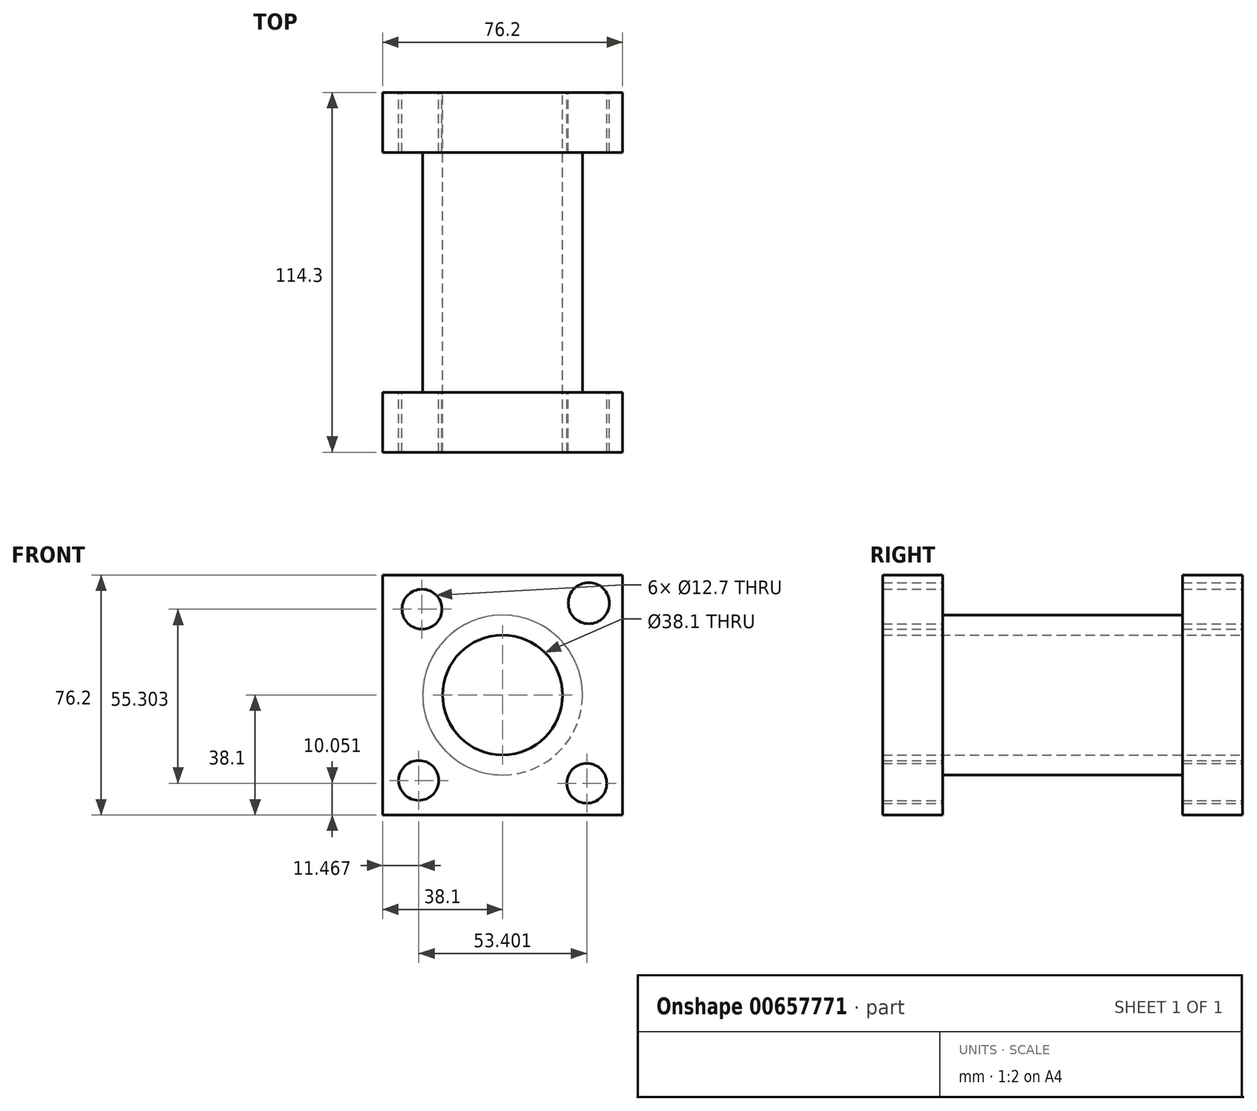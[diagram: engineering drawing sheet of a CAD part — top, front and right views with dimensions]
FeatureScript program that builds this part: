
annotation { "Feature Type Name" : "Feature", "Feature Type Description" : "" }
export const myFeature = defineFeature(function(context is Context, id is Id, definition is map)
    precondition{}
    {
        {
            var Q0;
            Q0=qCreatedBy(makeId("Front.planeOp"),FACE);
            var sketch = newSketch(context, id + "F0", { "sketchPlane" : qUnion([Q0])});
            skLineSegment(sketch, "E0.bottom", {"start": v(38.1, 38.1) * mm, "end": v(-38.1, 38.1) * mm});
            skLineSegment(sketch, "E0.top", {"start": v(38.1, -38.1) * mm, "end": v(-38.1, -38.1) * mm});
            skLineSegment(sketch, "E0.left", {"start": v(38.1, 38.1) * mm, "end": v(38.1, -38.1) * mm});
            skLineSegment(sketch, "E0.right", {"start": v(-38.1, 38.1) * mm, "end": v(-38.1, -38.1) * mm});
            skPoint(sketch, "E0.middle", {"position": v(0, 0) * mm});
            skSolve(sketch);
        }
        {
            var Q0;
            Q0 = qSketchRegion(id + "F0", true);
            extrude(context, id + "F1", {"entities" : qUnion([Q0]), "depth" : 19.05 * mm, "offsetDistance" : 25.4 * mm});
        }
        {
            var Q0;
            Q0=makeQuery(id+"F1.opExtrude","CAP_FACE",FACE,{"disambiguationData":[OSD([sQuery(id+"F0.wireOp",EDGE,"E0.bottom"),sQuery(id+"F0.wireOp",EDGE,"E0.top"),sQuery(id+"F0.wireOp",EDGE,"E0.left"),sQuery(id+"F0.wireOp",EDGE,"E0.right")])],"isStart":false});
            var sketch = newSketch(context, id + "F2", { "sketchPlane" : qUnion([Q0])});
            skCircle(sketch, "E1", {"center": v(0, 0) * mm, "radius": 19.05 * mm});
            skSolve(sketch);
        }
        {
            var Q0;
            Q0=makeQuery(id+"F2.imprint","IMPRINT",FACE,{"disambiguationData":[TD([[makeQuery(id+"F2.imprint","IMPRINT",EDGE,{"derivedFrom":sQuery(id+"F2.wireOp",EDGE,"E1")}),1.0]])]});
            extrude(context, id + "F3", {"entities" : qUnion([Q0]), "operationType" : NewBodyOperationType.ADD, "depth" : 25.4 * mm, "offsetDistance" : 25.4 * mm});
        }
        {
            var Q0;
            Q0=makeQuery(id+"F3.opExtrude","CAP_FACE",FACE,{"disambiguationData":[OSD([sQuery(id+"F2.wireOp",EDGE,"E1")])],"isStart":false});
            var sketch = newSketch(context, id + "F4", { "sketchPlane" : qUnion([Q0])});
            skSolve(sketch);
        }
        {
            var Q0;
            Q0 = qSketchRegion(id + "F4", true);
            var Q1;
            Q1=makeQuery(id+"F4.imprint","IMPRINT",FACE,{"disambiguationData":[TD([[makeQuery(id+"F4.imprint","IMPRINT",EDGE,{"derivedFrom":makeQuery(id+"F3.opExtrude","CAP_EDGE",EDGE,{"disambiguationData":[OSD([sQuery(id+"F2.wireOp",EDGE,"E1")])],"isStart":false})}),1.0]])]});
            extrude(context, id + "F5", {"entities" : qUnion([Q0, Q1]), "operationType" : NewBodyOperationType.ADD, "depth" : 50.8 * mm, "offsetDistance" : 25.4 * mm});
        }
        {
            var Q0;
            Q0=makeQuery(id+"F5.opExtrude","CAP_FACE",FACE,{"disambiguationData":[OSD([sQuery(id+"F2.wireOp",EDGE,"E1")])],"isStart":false});
            var sketch = newSketch(context, id + "F6", { "sketchPlane" : qUnion([Q0])});
            skLineSegment(sketch, "E2.bottom", {"start": v(-38.1, -38.1) * mm, "end": v(38.1, -38.1) * mm});
            skLineSegment(sketch, "E2.top", {"start": v(-38.1, 38.1) * mm, "end": v(38.1, 38.1) * mm});
            skLineSegment(sketch, "E2.left", {"start": v(-38.1, -38.1) * mm, "end": v(-38.1, 38.1) * mm});
            skLineSegment(sketch, "E2.right", {"start": v(38.1, -38.1) * mm, "end": v(38.1, 38.1) * mm});
            skPoint(sketch, "E2.middle", {"position": v(0, 0) * mm});
            skSolve(sketch);
        }
        {
            var Q0;
            Q0 = qSketchRegion(id + "F6", true);
            extrude(context, id + "F7", {"entities" : qUnion([Q0]), "operationType" : NewBodyOperationType.ADD, "depth" : 19.05 * mm, "offsetDistance" : 25.4 * mm});
        }
        {
            var Q0;
            Q0=makeQuery(id+"F7.opExtrude","CAP_FACE",FACE,{"disambiguationData":[OSD([sQuery(id+"F6.wireOp",EDGE,"E2.bottom"),sQuery(id+"F6.wireOp",EDGE,"E2.top"),sQuery(id+"F6.wireOp",EDGE,"E2.left"),sQuery(id+"F6.wireOp",EDGE,"E2.right")])],"isStart":true});
            var sketch = newSketch(context, id + "F8", { "sketchPlane" : qUnion([Q0])});
            skCircle(sketch, "E3", {"center": v(0, 0) * mm, "radius": 25.4 * mm});
            skSolve(sketch);
        }
        {
            var Q0;
            Q0 = qSketchRegion(id + "F8", true);
            extrude(context, id + "F9", {"entities" : qUnion([Q0]), "operationType" : NewBodyOperationType.ADD, "depth" : 76.2 * mm, "offsetDistance" : 25.4 * mm});
        }
        {
            var Q0;
            Q0=makeQuery(id+"F1.opExtrude","CAP_FACE",FACE,{"disambiguationData":[OSD([sQuery(id+"F0.wireOp",EDGE,"E0.bottom"),sQuery(id+"F0.wireOp",EDGE,"E0.top"),sQuery(id+"F0.wireOp",EDGE,"E0.left"),sQuery(id+"F0.wireOp",EDGE,"E0.right")])],"isStart":true});
            var sketch = newSketch(context, id + "F10", { "sketchPlane" : qUnion([Q0])});
            skCircle(sketch, "E4", {"center": v(0, 0) * mm, "radius": 19.05 * mm});
            skSolve(sketch);
        }
        {
            var Q0;
            Q0=makeQuery(id+"F10.imprint","IMPRINT",FACE,{"disambiguationData":[TD([[makeQuery(id+"F10.imprint","IMPRINT",EDGE,{"derivedFrom":sQuery(id+"F10.wireOp",EDGE,"E4")}),1.0]])]});
            extrude(context, id + "F11", {"entities" : qUnion([Q0]), "operationType" : NewBodyOperationType.REMOVE, "oppositeDirection" : true, "depth" : 114.3 * mm, "offsetDistance" : 25.4 * mm});
        }
        {
            var Q0;
            Q0=makeQuery(id+"F1.opExtrude","CAP_FACE",FACE,{"disambiguationData":[OSD([sQuery(id+"F0.wireOp",EDGE,"E0.bottom"),sQuery(id+"F0.wireOp",EDGE,"E0.top"),sQuery(id+"F0.wireOp",EDGE,"E0.left"),sQuery(id+"F0.wireOp",EDGE,"E0.right")])],"isStart":true});
            var sketch = newSketch(context, id + "F12", { "sketchPlane" : qUnion([Q0])});
            skCircle(sketch, "E5", {"center": v(25.59, 27.25) * mm, "radius": 6.35 * mm});
            skSolve(sketch);
        }
        {
            var Q0;
            Q0=makeQuery(id+"F12.imprint","IMPRINT",FACE,{"disambiguationData":[TD([[makeQuery(id+"F12.imprint","IMPRINT",EDGE,{"derivedFrom":sQuery(id+"F12.wireOp",EDGE,"E5")}),-1.0]])]});
            var sketch = newSketch(context, id + "F13", { "sketchPlane" : qUnion([Q0])});
            skCircle(sketch, "E6", {"center": v(-27.41, 29.17) * mm, "radius": 6.54 * mm});
            skCircle(sketch, "E7", {"center": v(-26.77, -28.05) * mm, "radius": 6.35 * mm});
            skCircle(sketch, "E8", {"center": v(26.63, -27.13) * mm, "radius": 6.35 * mm});
            skSolve(sketch);
        }
        {
            var Q0;
            Q0=makeQuery(id+"F12.imprint","IMPRINT",FACE,{"disambiguationData":[TD([[makeQuery(id+"F12.imprint","IMPRINT",EDGE,{"derivedFrom":sQuery(id+"F12.wireOp",EDGE,"E5")}),1.0]])]});
            extrude(context, id + "F14", {"entities" : qUnion([Q0]), "operationType" : NewBodyOperationType.REMOVE, "oppositeDirection" : true, "depth" : 114.3 * mm, "offsetDistance" : 25.4 * mm});
        }
        {
            var Q0;
            Q0 = qSketchRegion(id + "F13", true);
            extrude(context, id + "F15", {"entities" : qUnion([Q0]), "operationType" : NewBodyOperationType.REMOVE, "oppositeDirection" : true, "depth" : 127 * mm, "offsetDistance" : 25.4 * mm});
        }
    });
